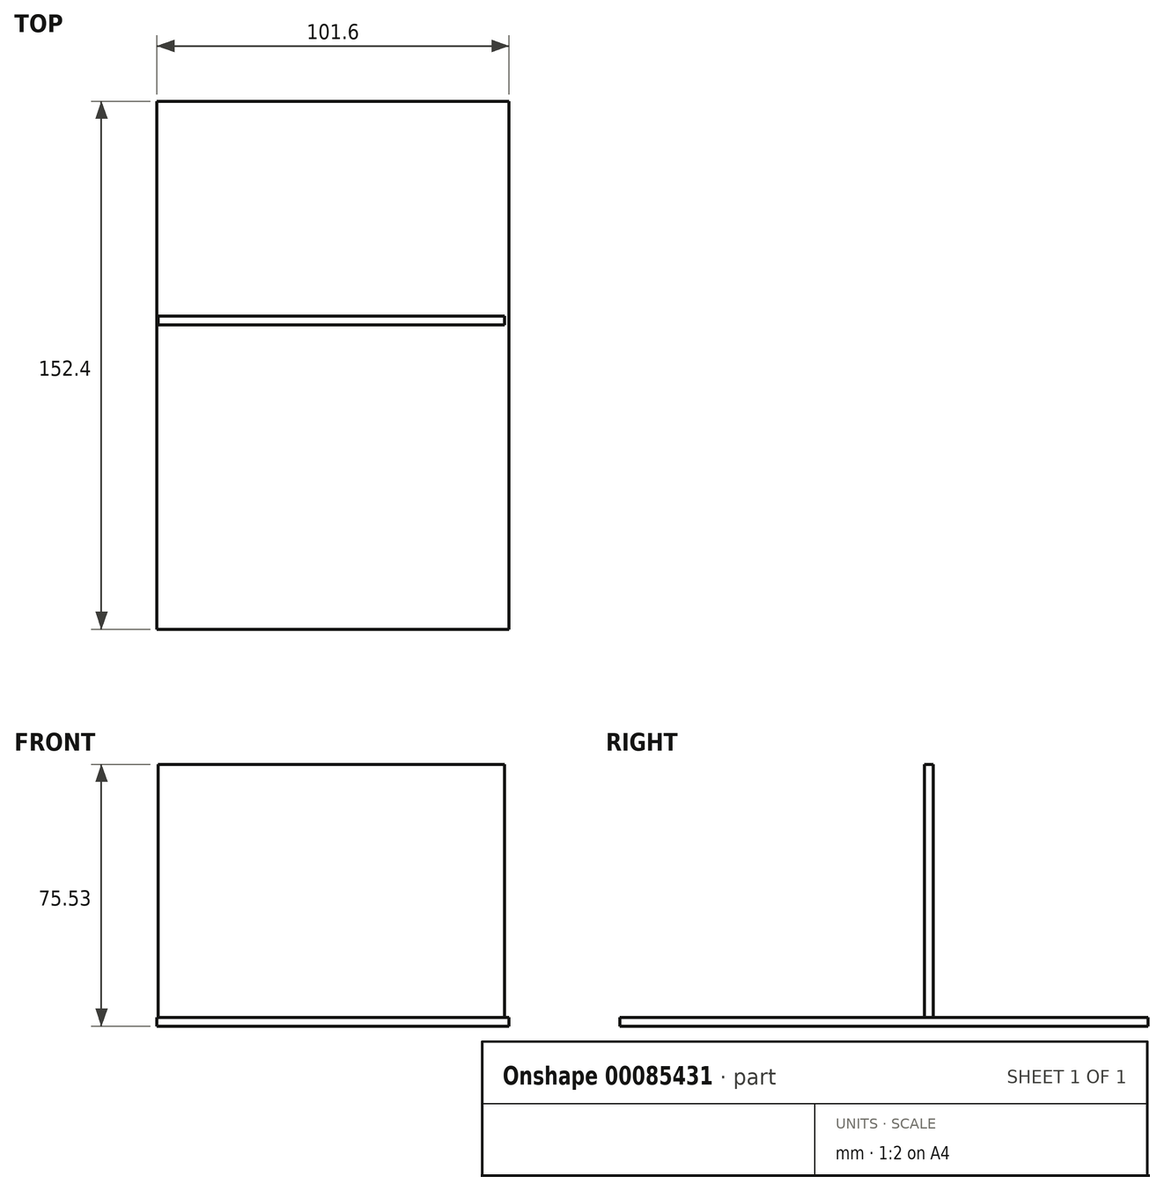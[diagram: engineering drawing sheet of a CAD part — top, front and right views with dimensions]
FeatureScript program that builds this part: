
annotation { "Feature Type Name" : "Feature", "Feature Type Description" : "" }
export const myFeature = defineFeature(function(context is Context, id is Id, definition is map)
    precondition{}
    {
        {
            var Q0;
            Q0=qCreatedBy(makeId("Top.planeOp"),FACE);
            var sketch = newSketch(context, id + "F0", { "sketchPlane" : qUnion([Q0])});
            skLineSegment(sketch, "E0", {"start": v(-53.82, -90.38) * mm, "end": v(47.78, -90.38) * mm});
            skLineSegment(sketch, "E1", {"start": v(47.78, -90.38) * mm, "end": v(47.78, 62.02) * mm});
            skLineSegment(sketch, "E2", {"start": v(47.78, 62.02) * mm, "end": v(-53.82, 62.02) * mm});
            skLineSegment(sketch, "E3", {"start": v(-53.82, 62.02) * mm, "end": v(-53.82, -90.38) * mm});
            skSolve(sketch);
        }
        {
            var Q0;
            Q0 = qSketchRegion(id + "F0", true);
            extrude(context, id + "F1", {"entities" : qUnion([Q0]), "depth" : 2.54 * mm});
        }
        {
            var Q0;
            Q0=qCreatedBy(makeId("Front.planeOp"),FACE);
            var sketch = newSketch(context, id + "F2", { "sketchPlane" : qUnion([Q0])});
            skLineSegment(sketch, "E4.bottom", {"start": v(-53.53, 0) * mm, "end": v(46.44, 0) * mm});
            skLineSegment(sketch, "E4.top", {"start": v(-53.53, 75.53) * mm, "end": v(46.44, 75.53) * mm});
            skLineSegment(sketch, "E4.left", {"start": v(-53.53, 0) * mm, "end": v(-53.53, 75.53) * mm});
            skLineSegment(sketch, "E4.right", {"start": v(46.44, 0) * mm, "end": v(46.44, 75.53) * mm});
            skSolve(sketch);
        }
        {
            var Q0;
            Q0 = qSketchRegion(id + "F2", true);
            extrude(context, id + "F3", {"entities" : qUnion([Q0]), "operationType" : NewBodyOperationType.ADD, "depth" : 2.54 * mm});
        }
    });
